# Revit family: GP118-sw
name_source: partatom
category: Communication Devices
revit_build: Autodesk Revit Architecture 2012 (Build: 20110309_2315(x64)
units: mm (PartAtom-declared; Revit-internal decimal feet)

## types (1)
- GP118-sw
    Default Elevation = 0 mm
    Depth = 771.5 mm
    Description = Vented 18" Subwoofer
    Enclosure Material = Black Finish
    Front Handle Offset = 195 mm
    Grill Depth = 52.1 mm
    Grill Width = 621.9 mm
    Grille Material = Black Grille
    Height = 510.5 mm
    Impedance = 8
    Manufacturer = QSC Audio Products, LLC
    Manufacturer URL = www.qscaudio.com
    Model = GP118-sw
    Overall Depth = 771.5 mm
    Overall Height = 510.5 mm
    Overall Width = 655.3 mm
    Power Handling = 1700
    Product Documentation Link = http://qscmarketing.com
    Product Page URL = http://qsc.com
    Rear Handle Offset = 599.5 mm
    Regulatory Compliance = RoHS
    SPL Max = 129
    Sensitivity = 98
    URL = http://qsc.com
    Weight Dimensional (kg) = 54.9
    Weight Dimensional (lb) = 121
    Weight Product (kg) = 50.3
    Weight Product (lb) = 111
    Width = 655.3 mm

## geometry (parser evidence)
native form markers: Blend x2, Sweep x1
no freeform markers — native parametric forms only
